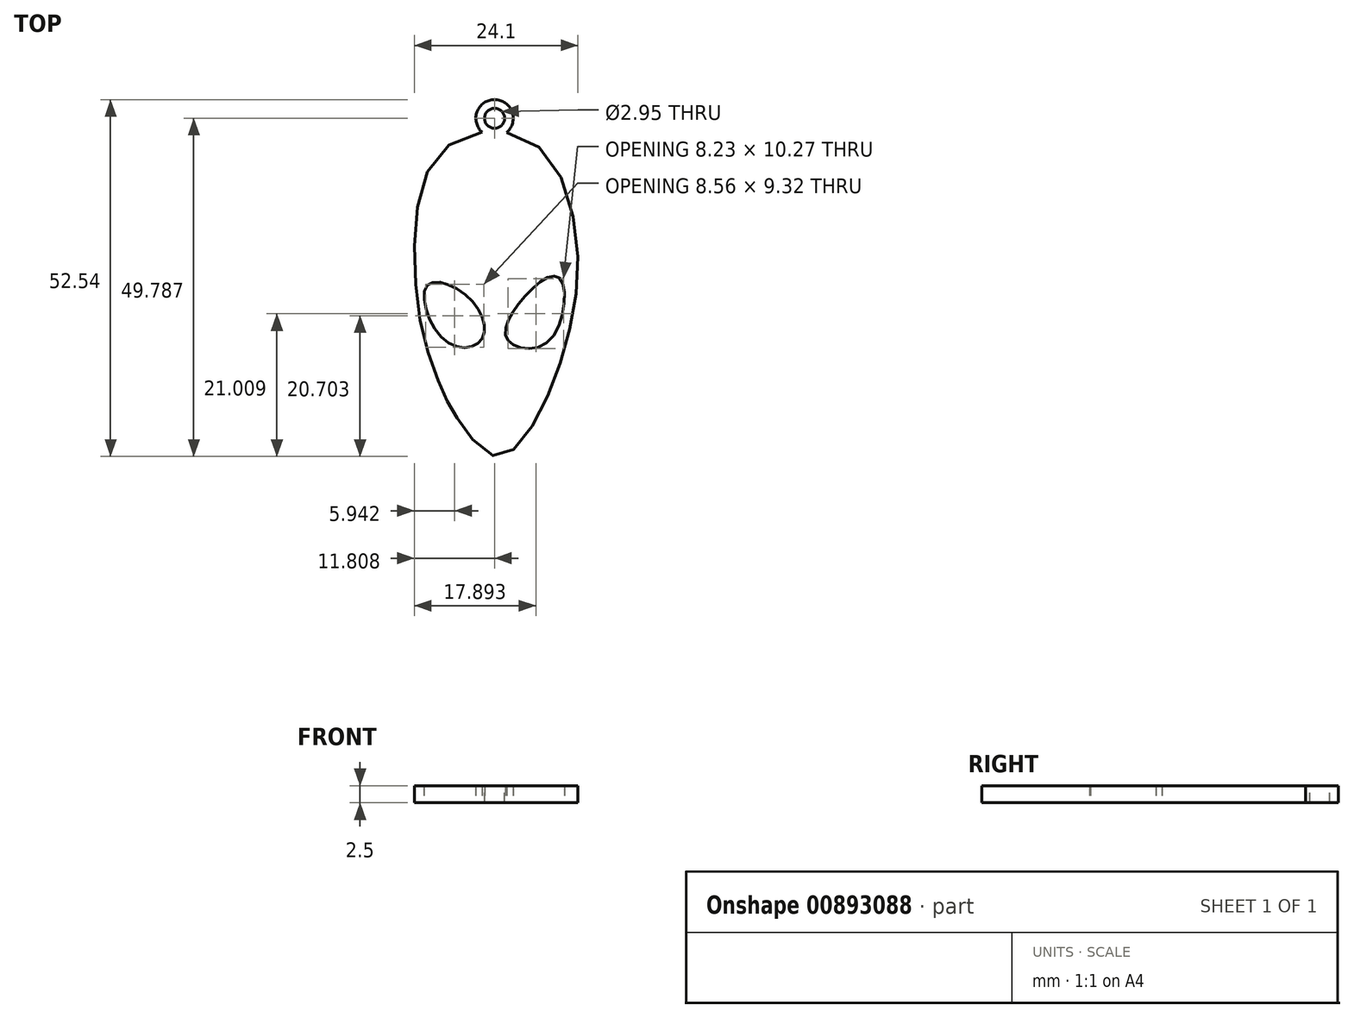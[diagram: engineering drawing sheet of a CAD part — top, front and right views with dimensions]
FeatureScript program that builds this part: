
annotation { "Feature Type Name" : "Feature", "Feature Type Description" : "" }
export const myFeature = defineFeature(function(context is Context, id is Id, definition is map)
    precondition{}
    {
        {
            var Q0;
            Q0=qCreatedBy(makeId("Top.planeOp"),FACE);
            var sketch = newSketch(context, id + "F0", { "sketchPlane" : qUnion([Q0])});
            skFitSpline(sketch, "E0", {"points": [v(0, 14.83) * mm, v(4.45, 28.25) * mm, v(17.1, 29.37) * mm, v(23.9, 14.8) * mm, v(22.45, 0) * mm, v(17.5, -12.3) * mm, v(11.97, -17.06) * mm, v(6.63, -12.03) * mm, v(4.45, -8.11) * mm, v(1.48, 0) * mm, v(0, 14.83) * mm]});
            skFitSpline(sketch, "E1", {"points": [v(1.88, 8.11) * mm, v(8.4, 5.87) * mm, v(9.8, 0) * mm, v(4.45, 0) * mm, v(1.88, 8.11) * mm]});
            skFitSpline(sketch, "E2", {"points": [v(13.75, 0) * mm, v(15.73, 5.87) * mm, v(21.26, 9.23) * mm, v(19.88, 0) * mm, v(13.75, 0) * mm]});
            skCircle(sketch, "E3", {"center": v(11.78, 32.7) * mm, "radius": 2.75 * mm});
            skSolve(sketch);
        }
        {
            var Q0;
            Q0 = qSketchRegion(id + "F0", true);
            extrude(context, id + "F1", {"entities" : qUnion([Q0]), "depth" : 2.5 * mm, "offsetDistance" : 25 * mm});
        }
        {
            var Q0;
            Q0=makeQuery(id+"F1.opExtrude","CAP_FACE",FACE,{"disambiguationData":[OSD([sQuery(id+"F0.wireOp",EDGE,"E0"),sQuery(id+"F0.wireOp",EDGE,"E1"),sQuery(id+"F0.wireOp",EDGE,"E2"),sQuery(id+"F0.wireOp",EDGE,"E3")])],"isStart":false});
            var sketch = newSketch(context, id + "F2", { "sketchPlane" : qUnion([Q0])});
            skCircle(sketch, "E4", {"center": v(11.78, 32.7) * mm, "radius": 1.48 * mm});
            skSolve(sketch);
        }
        {
            var Q0;
            Q0 = qSketchRegion(id + "F2", true);
            extrude(context, id + "F3", {"entities" : qUnion([Q0]), "operationType" : NewBodyOperationType.REMOVE, "oppositeDirection" : true, "depth" : 25 * mm, "offsetDistance" : 25 * mm});
        }
    });
